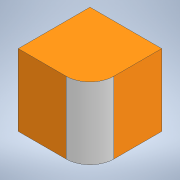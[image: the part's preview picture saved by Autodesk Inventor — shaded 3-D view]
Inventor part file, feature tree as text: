
AUTODESK INVENTOR PART (.ipt)
format: ipt  version: 2022 (Build 260153000, 153)  size: 94,208 bytes
history: native  units: mm
features: extrude x1, fillet x1, sketch x1
ambient origin geometry x8: Origin, YZ Plane, XZ Plane, XY Plane, X Axis, Y Axis, Z Axis, Center Point
bodies: Solid1 (feature_tree)
feature tree (3):
  extrude  "Extrusion1"  Depth=15.0mm
  fillet  "Fillet1"  Radius=15.0mm
  sketch  "Sketch1"  dims[d0=15.0mm d1=15.0mm d2=15.0mm d3=0.0mm d4=5.0mm]
